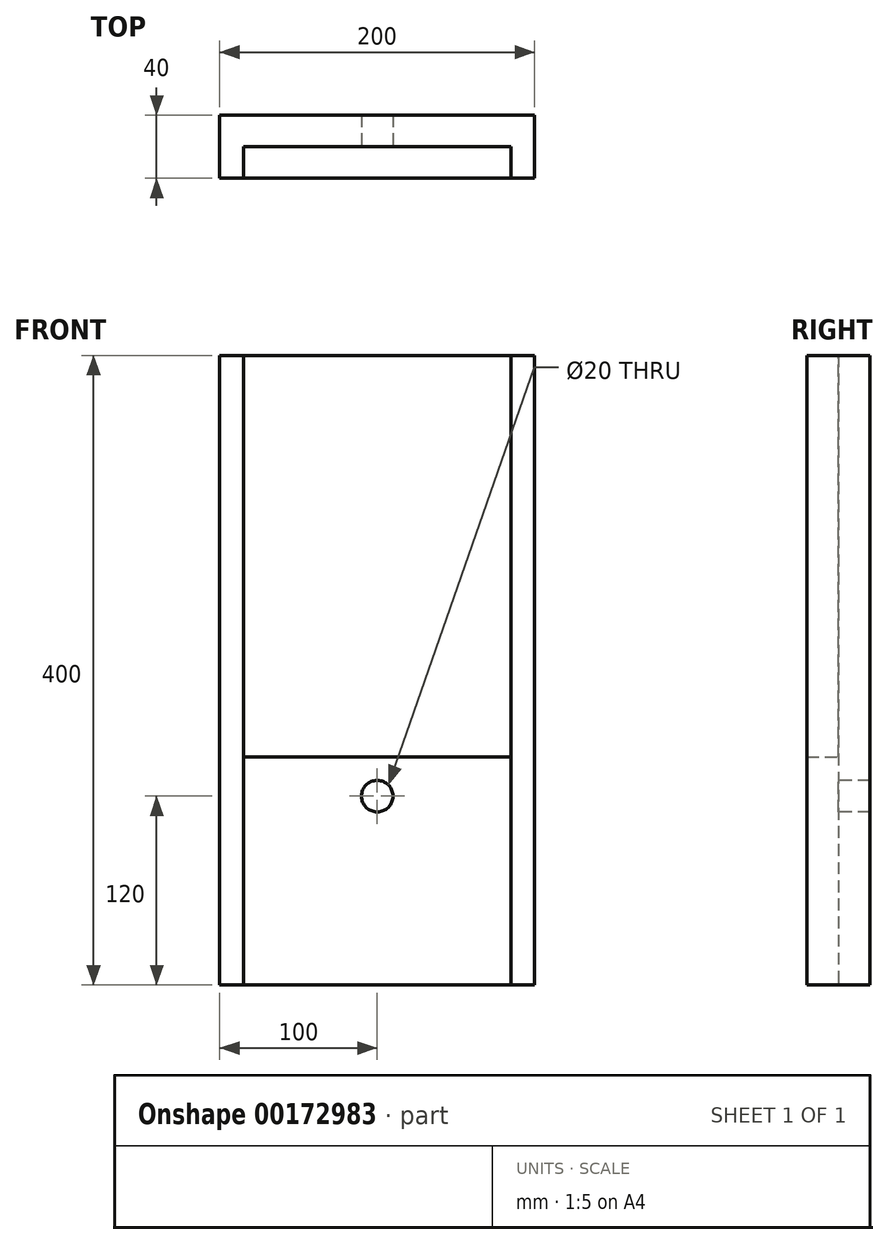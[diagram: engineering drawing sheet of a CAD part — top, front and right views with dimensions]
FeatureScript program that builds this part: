
annotation { "Feature Type Name" : "Feature", "Feature Type Description" : "" }
export const myFeature = defineFeature(function(context is Context, id is Id, definition is map)
    precondition{}
    {
        {
            var Q0;
            Q0=qCreatedBy(makeId("Top.planeOp"),FACE);
            var sketch = newSketch(context, id + "F0", { "sketchPlane" : qUnion([Q0])});
            skLineSegment(sketch, "E0", {"start": v(0, 40) * mm, "end": v(100, 40) * mm});
            skLineSegment(sketch, "E1", {"start": v(100, 40) * mm, "end": v(100, 0) * mm});
            skLineSegment(sketch, "E2", {"start": v(100, 0) * mm, "end": v(85, 0) * mm});
            skLineSegment(sketch, "E3", {"start": v(85, 0) * mm, "end": v(85, 20) * mm});
            skLineSegment(sketch, "E4", {"start": v(85, 20) * mm, "end": v(0, 20) * mm});
            skLineSegment(sketch, "E5", {"start": v(0, 40) * mm, "end": v(0, 0) * mm, "construction": true});
            skLineSegment(sketch, "E6.MirrorCS", {"start": v(0, 40) * mm, "end": v(-100, 40) * mm});
            skLineSegment(sketch, "E7.MirrorCS", {"start": v(-100, 40) * mm, "end": v(-100, 0) * mm});
            skLineSegment(sketch, "E8.MirrorCS", {"start": v(-100, 0) * mm, "end": v(-85, 0) * mm});
            skLineSegment(sketch, "E9.MirrorCS", {"start": v(-85, 20) * mm, "end": v(0, 20) * mm});
            skLineSegment(sketch, "E10.MirrorCS", {"start": v(-85, 0) * mm, "end": v(-85, 20) * mm});
            skSolve(sketch);
        }
        {
            var Q0;
            Q0 = qSketchRegion(id + "F0", true);
            extrude(context, id + "F1", {"entities" : qUnion([Q0]), "depth" : 280 * mm, "hasSecondDirection" : true, "secondDirectionOppositeDirection" : true, "secondDirectionDepth" : 120 * mm});
        }
        {
            var Q0;
            Q0=makeQuery(id+"F1.opExtrude","SWEPT_FACE",FACE,{"disambiguationData":[OSD([sQuery(id+"F0.wireOp",EDGE,"E4"),sQuery(id+"F0.wireOp",EDGE,"E9.MirrorCS")])]});
            var sketch = newSketch(context, id + "F2", { "sketchPlane" : qUnion([Q0])});
            skCircle(sketch, "E11", {"center": v(0, 0) * mm, "radius": 10 * mm});
            skSolve(sketch);
        }
        {
            var Q0;
            Q0 = qSketchRegion(id + "F2", true);
            extrude(context, id + "F3", {"entities" : qUnion([Q0]), "operationType" : NewBodyOperationType.REMOVE, "oppositeDirection" : true, "depth" : 20 * mm});
        }
        {
            var Q0;
            Q0=makeQuery(id+"F1.opExtrude","CAP_FACE",FACE,{"disambiguationData":[OSD([sQuery(id+"F0.wireOp",EDGE,"E0"),sQuery(id+"F0.wireOp",EDGE,"E1"),sQuery(id+"F0.wireOp",EDGE,"E2"),sQuery(id+"F0.wireOp",EDGE,"E3"),sQuery(id+"F0.wireOp",EDGE,"E4"),sQuery(id+"F0.wireOp",EDGE,"E6.MirrorCS"),sQuery(id+"F0.wireOp",EDGE,"E7.MirrorCS"),sQuery(id+"F0.wireOp",EDGE,"E8.MirrorCS"),sQuery(id+"F0.wireOp",EDGE,"E9.MirrorCS"),sQuery(id+"F0.wireOp",EDGE,"E10.MirrorCS")])],"isStart":false});
            var sketch = newSketch(context, id + "F4", { "sketchPlane" : qUnion([Q0])});
            skLineSegment(sketch, "E12", {"start": v(-85, 20) * mm, "end": v(-85, 0) * mm});
            skLineSegment(sketch, "E13", {"start": v(-85, 0) * mm, "end": v(85, 0) * mm});
            skLineSegment(sketch, "E14", {"start": v(85, 0) * mm, "end": v(85, 20) * mm});
            skLineSegment(sketch, "E15", {"start": v(85, 20) * mm, "end": v(-85, 20) * mm});
            skSolve(sketch);
        }
        {
            var Q0;
            Q0 = qSketchRegion(id + "F4", true);
            extrude(context, id + "F5", {"entities" : qUnion([Q0]), "oppositeDirection" : true, "depth" : 255 * mm});
        }
    });
